# Revit family: Double_Check_Valve_Assemblies-WATTS-(050-100_LF007-QT, 050-100_LF007-QT-S)_Series
name_source: partatom
category: Pipe Accessories
units: mm (PartAtom-declared; Revit-internal decimal feet)

## family parameters
Always vertical = Yes
Cut with Voids When Loaded = No
OmniClass Number = 23.65.55.14.21
OmniClass Title = Non-Return Valves for Liquid Services
Part Type = Valve - Breaks Into
Round Connector Dimension = Use Radius
Shared = No
Work Plane-Based = No

## types (6) — shared parameters
Assembly Code = D2090900
Body_Angle = 45.00°
Connection Type = NPT Connection
Country = United States
Description = Lead Free* Double Check Valve Assembly Backflow Preventers with Freeze Sensor
FZ Freeze Sensor = No
Finish = Metal-WATTS-Cast Copper Silicon Alloy
Flow Rate = 7.5 fps / 2.3 mps
IAPMO Compliance = ASSE Standard 1015, AWWA Standard C510
IAPMO PS31, CSA B64.5
LF Without shutoff valves = No
Manufacturer = WATTS
Manufacturer Product Line = Backflow Prevention
Material = Metal-Watts-Cast Copper Silicon Alloy
Pressure Rating = 175.00 psi
Product Documentation Link = https://www.watts.com
Product Page URL = https://www.watts.com
Region = North America
Revised Date = 10/11/2023
STR_Angle = 45.00°
TC_Body_Hieght = 15/16"
TC_Body_Rad = 13/32"
TC_Boss_Rad = 5/16"
TC_In_Thd_Length = 11/32"
TC_In_Thd_Rad = 7/32"
TC_Out_Thd_Length = 1/2"
TC_Out_Thd_Rad = 7/32"
Temperature Range = 175 psi (12.1 bar)
U Union connections = No
URL = http://www.watts.com
W/Press** Press inlet x press outlet = No

## per-type parameters (varying)
- LF007-QT-S - 0.5": A Dimension=10"; As Dimension=13"; B Dimension=3 5/8"; BV1_OAL=2 1/2"; BV1_Stem_Dist=1 1/4"; BV2_OAL=2 1/2"; BV2_Stem_Dist=1 1/32"; BV_Body_Rad=19/32"; BV_Handle_Angle=30.00°; BV_Handle_CL_Angle=15/32"; BV_Handle_Hieght=3/8"; BV_Handle_Length=1 9/16"; BV_Handle_Thk=3/32"; BV_Handle_Width_Btm=-13/32"; BV_Handle_Width_Top=13/32"; BV_Stem_Hieght=1 5/32"; BV_Stem_Rad=11/32"; Body_IN_Angle=4 5/8"; Body_Rad=5/8"; Body_Retain_Rad=15/16"; Body_Step_Rad=15/32"; Body_Thd_Rad=7/16"; Bs Dimension=6"; C Dimension=2 7/16"; Connection Size=1/2"; Connection_Rad=0"; Cover_Dist=2 13/16"; Cover_Hieght=1 3/32"; Cover_Thk=17/32"; D Dimension=3"; F Dimension=5"; G Dimension=3 3/8"; In_Thd_Length=7/32"; Inlet Connection Description=1/2" Inlet Connection; Length=13"; Out_Thd_Length=11/32"; Outlet Connection Description=1/2" Outlet Connection; Pipe Connection Distance=2 17/32"; R Dimension=2 5/16"; S Copper silicon alloy strainer=Yes; STR_Flow_Rad=9/16"; STR_IN_Port=23/32"; STR_Main_Rad=11/16"; STR_Nipple_OAL=15/32"; STR_Nipple_Rad=7/16"; STR_OAL=2 17/32"; STR_Port_Length=3 19/32"; STR_Screen_Length=3 19/32"; Shipping Weight=5.50 lb; T Dimension=2 1/16"; TC1_Boss_Hieght=29/32"; TC1_Dist=21/32"; TC2_Boss_Hieght=29/32"; TC2_Dist=3 5/32"; TC3_Boss_Hieght=1 3/32"; TC3_Dist=5 3/8"; TC4_Boss_Hieght=29/32"; TC4_Dist=6 3/4"
- LF007-M3-QT-S - 0.75": A Dimension=11 1/8"; As Dimension=14 1/2"; B Dimension=4"; BV1_OAL=2 15/32"; BV1_Stem_Dist=1 7/16"; BV2_OAL=2 15/32"; BV2_Stem_Dist=1 7/32"; BV_Body_Rad=25/32"; BV_Handle_Angle=45.00°; BV_Handle_CL_Angle=21/32"; BV_Handle_Hieght=7/16"; BV_Handle_Length=1 21/32"; BV_Handle_Thk=1/8"; BV_Handle_Width_Btm=-7/16"; BV_Handle_Width_Top=7/16"; BV_Stem_Hieght=1 15/32"; BV_Stem_Rad=13/32"; Body_IN_Angle=5 9/32"; Body_Rad=27/32"; Body_Retain_Rad=27/32"; Body_Step_Rad=19/32"; Body_Thd_Rad=17/32"; Bs Dimension=6 1/8"; C Dimension=3 1/8"; Connection Size=3/4"; Connection_Rad=0"; Cover_Dist=2 29/32"; Cover_Hieght=1 1/4"; Cover_Thk=11/16"; D Dimension=3"; F Dimension=6 3/16"; G Dimension=3 7/16"; In_Thd_Length=11/32"; Inlet Connection Description=3/4" Inlet Connection; Length=14 1/2"; Out_Thd_Length=5/16"; Outlet Connection Description=3/4" Outlet Connection; Pipe Connection Distance=3 9/32"; R Dimension=2 1/8"; S Copper silicon alloy strainer=Yes; STR_Flow_Rad=5/8"; STR_IN_Port=27/32"; STR_Main_Rad=13/16"; STR_Nipple_OAL=3/32"; STR_Nipple_Rad=17/32"; STR_OAL=3 9/32"; STR_Port_Length=3 13/32"; STR_Screen_Length=3 13/32"; Shipping Weight=6.70 lb; T Dimension=1 15/16"; TC1_Boss_Hieght=31/32"; TC1_Dist=11/16"; TC2_Boss_Hieght=1 9/32"; TC2_Dist=3 23/32"; TC3_Boss_Hieght=1 13/32"; TC3_Dist=5 3/8"; TC4_Boss_Hieght=1 9/32"; TC4_Dist=7 25/32"
- LF007-M1-QT-S - 1": A Dimension=13 1/4"; As Dimension=17 15/16"; B Dimension=5 1/8"; BV1_OAL=2 7/8"; BV1_Stem_Dist=1 11/16"; BV2_OAL=2 7/8"; BV2_Stem_Dist=1 15/32"; BV_Body_Rad=15/16"; BV_Handle_Angle=45.00°; BV_Handle_CL_Angle=5/8"; BV_Handle_Hieght=7/16"; BV_Handle_Length=1 21/32"; BV_Handle_Thk=1/8"; BV_Handle_Width_Btm=-1/2"; BV_Handle_Width_Top=1/2"; BV_Stem_Hieght=1 3/4"; BV_Stem_Rad=15/32"; Body_IN_Angle=5 15/16"; Body_Rad=1 3/32"; Body_Retain_Rad=1 3/32"; Body_Step_Rad=7/8"; Body_Thd_Rad=21/32"; Bs Dimension=7 3/4"; C Dimension=4"; Connection Size=1"; Connection_Rad=1"; Cover_Dist=3 5/16"; Cover_Hieght=1 15/16"; Cover_Thk=11/16"; D Dimension=3 1/4"; F Dimension=7 1/2"; G Dimension=3 3/8"; In_Thd_Length=11/32"; Inlet Connection Description=1" Inlet Connection; Length=17 15/16"; Out_Thd_Length=5/16"; Outlet Connection Description=1" Outlet Connection; Pipe Connection Distance=4 1/2"; R Dimension=1 11/16"; S Copper silicon alloy strainer=Yes; STR_Flow_Rad=13/16"; STR_IN_Port=1 5/32"; STR_Main_Rad=1 1/32"; STR_Nipple_OAL=3/16"; STR_Nipple_Rad=21/32"; STR_OAL=4 1/2"; STR_Port_Length=3 1/2"; STR_Screen_Length=3 1/2"; Shipping Weight=14.00 lb; T Dimension=1 11/16"; TC1_Boss_Hieght=1 3/32"; TC1_Dist=13/16"; TC2_Boss_Hieght=1 15/32"; TC2_Dist=4 1/8"; TC3_Boss_Hieght=2 9/32"; TC3_Dist=6 1/8"; TC4_Boss_Hieght=1 15/32"; TC4_Dist=9 17/32"
- LF007-QT - 0.5": A Dimension=10"; As Dimension=13"; B Dimension=3 5/8"; BV1_OAL=2 1/2"; BV1_Stem_Dist=1 1/4"; BV2_OAL=2 1/2"; BV2_Stem_Dist=1 1/32"; BV_Body_Rad=19/32"; BV_Handle_Angle=30.00°; BV_Handle_CL_Angle=15/32"; BV_Handle_Hieght=3/8"; BV_Handle_Length=1 9/16"; BV_Handle_Thk=3/32"; BV_Handle_Width_Btm=-13/32"; BV_Handle_Width_Top=13/32"; BV_Stem_Hieght=1 5/32"; BV_Stem_Rad=11/32"; Body_IN_Angle=4 5/8"; Body_Rad=5/8"; Body_Retain_Rad=15/16"; Body_Step_Rad=15/32"; Body_Thd_Rad=7/16"; Bs Dimension=6"; C Dimension=2 7/16"; Connection Size=1/2"; Connection_Rad=0"; Cover_Dist=2 13/16"; Cover_Hieght=1 3/32"; Cover_Thk=17/32"; D Dimension=3"; F Dimension=5"; G Dimension=3 3/8"; In_Thd_Length=7/32"; Inlet Connection Description=1/2" Inlet Connection; Length=13"; Out_Thd_Length=11/32"; Outlet Connection Description=1/2" Outlet Connection; Pipe Connection Distance=0"; R Dimension=2 5/16"; S Copper silicon alloy strainer=No; STR_Flow_Rad=9/16"; STR_IN_Port=23/32"; STR_Main_Rad=11/16"; STR_Nipple_OAL=15/32"; STR_Nipple_Rad=7/16"; STR_OAL=2 17/32"; STR_Port_Length=3 19/32"; STR_Screen_Length=3 19/32"; Shipping Weight=4.50 lb; T Dimension=2 1/16"; TC1_Boss_Hieght=29/32"; TC1_Dist=21/32"; TC2_Boss_Hieght=29/32"; TC2_Dist=3 5/32"; TC3_Boss_Hieght=1 3/32"; TC3_Dist=5 3/8"; TC4_Boss_Hieght=29/32"; TC4_Dist=6 3/4"
- LF007-M3-QT - 0.75": A Dimension=11 1/8"; As Dimension=14 1/2"; B Dimension=4"; BV1_OAL=2 15/32"; BV1_Stem_Dist=1 7/16"; BV2_OAL=2 15/32"; BV2_Stem_Dist=1 7/32"; BV_Body_Rad=25/32"; BV_Handle_Angle=45.00°; BV_Handle_CL_Angle=21/32"; BV_Handle_Hieght=7/16"; BV_Handle_Length=1 21/32"; BV_Handle_Thk=1/8"; BV_Handle_Width_Btm=-7/16"; BV_Handle_Width_Top=7/16"; BV_Stem_Hieght=1 15/32"; BV_Stem_Rad=13/32"; Body_IN_Angle=5 9/32"; Body_Rad=27/32"; Body_Retain_Rad=27/32"; Body_Step_Rad=19/32"; Body_Thd_Rad=17/32"; Bs Dimension=6 1/8"; C Dimension=3 1/8"; Connection Size=3/4"; Connection_Rad=0"; Cover_Dist=2 29/32"; Cover_Hieght=1 1/4"; Cover_Thk=11/16"; D Dimension=3"; F Dimension=6 3/16"; G Dimension=3 7/16"; In_Thd_Length=11/32"; Inlet Connection Description=3/4" Inlet Connection; Length=14 1/2"; Out_Thd_Length=5/16"; Outlet Connection Description=3/4" Outlet Connection; Pipe Connection Distance=0"; R Dimension=2 1/8"; S Copper silicon alloy strainer=No; STR_Flow_Rad=5/8"; STR_IN_Port=27/32"; STR_Main_Rad=13/16"; STR_Nipple_OAL=3/32"; STR_Nipple_Rad=17/32"; STR_OAL=3 9/32"; STR_Port_Length=3 13/32"; STR_Screen_Length=3 13/32"; Shipping Weight=5.00 lb; T Dimension=1 15/16"; TC1_Boss_Hieght=31/32"; TC1_Dist=11/16"; TC2_Boss_Hieght=1 9/32"; TC2_Dist=3 23/32"; TC3_Boss_Hieght=1 13/32"; TC3_Dist=5 3/8"; TC4_Boss_Hieght=1 9/32"; TC4_Dist=7 25/32"
- LF007-M1-QT - 1": A Dimension=13 1/4"; As Dimension=17 15/16"; B Dimension=5 1/8"; BV1_OAL=2 7/8"; BV1_Stem_Dist=1 11/16"; BV2_OAL=2 7/8"; BV2_Stem_Dist=1 15/32"; BV_Body_Rad=15/16"; BV_Handle_Angle=45.00°; BV_Handle_CL_Angle=5/8"; BV_Handle_Hieght=7/16"; BV_Handle_Length=1 21/32"; BV_Handle_Thk=1/8"; BV_Handle_Width_Btm=-1/2"; BV_Handle_Width_Top=1/2"; BV_Stem_Hieght=1 3/4"; BV_Stem_Rad=15/32"; Body_IN_Angle=5 15/16"; Body_Rad=1 3/32"; Body_Retain_Rad=1 3/32"; Body_Step_Rad=7/8"; Body_Thd_Rad=21/32"; Bs Dimension=7 3/4"; C Dimension=4"; Connection Size=1"; Connection_Rad=1"; Cover_Dist=3 5/16"; Cover_Hieght=1 15/16"; Cover_Thk=11/16"; D Dimension=3 1/4"; F Dimension=7 1/2"; G Dimension=3 3/8"; In_Thd_Length=11/32"; Inlet Connection Description=1" Inlet Connection; Length=17 15/16"; Out_Thd_Length=5/16"; Outlet Connection Description=1" Outlet Connection; Pipe Connection Distance=0"; R Dimension=1 11/16"; S Copper silicon alloy strainer=No; STR_Flow_Rad=13/16"; STR_IN_Port=1 5/32"; STR_Main_Rad=1 1/32"; STR_Nipple_OAL=3/16"; STR_Nipple_Rad=21/32"; STR_OAL=4 1/2"; STR_Port_Length=3 1/2"; STR_Screen_Length=3 1/2"; Shipping Weight=12.00 lb; T Dimension=1 11/16"; TC1_Boss_Hieght=1 3/32"; TC1_Dist=13/16"; TC2_Boss_Hieght=1 15/32"; TC2_Dist=4 1/8"; TC3_Boss_Hieght=2 9/32"; TC3_Dist=6 1/8"; TC4_Boss_Hieght=1 15/32"; TC4_Dist=9 17/32"

note: column(s) folded — value = type name in every type: Model

## geometry (parser evidence)
native form markers: Sweep x8
no freeform markers — native parametric forms only
